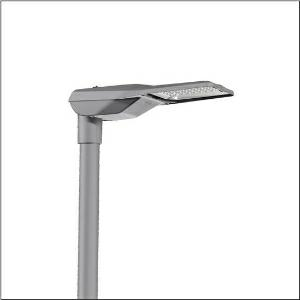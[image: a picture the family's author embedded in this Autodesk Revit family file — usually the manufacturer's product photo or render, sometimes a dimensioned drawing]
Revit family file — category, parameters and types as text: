
# Revit family: streetlight_sl_21_mini___p0_8ab_5xe2r33s08gb_ab20
name_source: partatom
category: Lighting Fixtures
units: mm (PartAtom-declared; Revit-internal decimal feet)

## family parameters
Cut with Voids When Loaded = No
Host = Face
Light Source = No
Part Type = Normal
Room Calculation Point = No
Round Connector Dimension = Use Diameter
Shared = No

## types (1)
- --- (1 x LED, 5160 lm, 40.4 W, 3000K)
    Apparent Load = 40 VA
    CIE Flux Codes = 36 71 98 100 100
    Color Rendering = 70
    Color Temperature = 3000K
    Default Elevation = 1800 mm
    Description = Streetlight SL 21 mini, mast luminaire, primary light control with lens, of PMMA, primary optical cover: cover, of toughened safety glass, transparent, light distribution: P0.8aB, light emission: direct distribution, primary light characteristic: asymmetric, installation type: post-top, side-entry, LED, High Power LED, rated luminous flux: 5.160lm, luminous efficacy: 128lm/W, light colour: 730, colour temperature: 3000K, control gear: D4i, control: pre-setting: logarithmic dimming characteristic, flexible luminous flux parameterisation, time-dependent luminous flux control, constant luminous flux control, overheat protection, mains connection: 220..240V, AC, 50/60Hz, start of lifetime: 40W, end of service life: 41W, reduction: 19W, luminaire housing, of diecast aluminium, powder-coated, Siteco® metallic grey (DB 702S), corrosivity category C5 mid according to DIN EN ISO 12944, multi-level sealing system, sealing non-destructively replaceable, inclination adjustable: 0°, 5°, 10°, 15°, please order mast flange separately, length: 628mm, width: 235mm, height: 110mm, mast flange for spigot size: 42mm (side-entry): 5XC10008XM4, 60/48mm (side-entry/post-top): 5XC10108XM2, 76/60mm (side-entry/post-top): 5XC10108XM1, mounting height: 4..8m, Smart Interface above, protection rating (complete): IP66, insulation class (complete): insulation class II (safety insulation), certification: CE, ENEC, ENEC+, VDE, impact resistance: IK10, permissible operating ambient temperature for outdoor applications: -40..+50°C, standard-compliant lighting for roads and squares, packaging unit: 1 piece

Light Distribution: P0.8aB
    Height = 110 mm
    Lamp = 1 x LED
    Lamp Light Flux = 5160 lm
    Lamp Power = 40.4 W
    Lamp count = 1
    Length = 625 mm
    Luminous efficacy = 128 lm/W
    Manufacturer = Siteco
    ModVariant = No
    Model = 5XE2R33S08GB
    Number of Poles = 1
    OnlyDefault = Yes
    Power Factor = 1
    Product Name = Streetlight SL 21 mini | P0.8aB
    Product group = mast luminaire | pylon top
    ProductGroupID = 6100
    Protection Class = Protection class II
    Protection Degree = IP 66
    RLX_Detail_Level = 1
    RLX_Emergency_Light_Flux = 0 lm
    RLX_Emergency_Type = 0
    RLX_Emergency_Type_DB = No
    RlxData = <blob elided: 91781 chars, md5=c8cf1a39>
    Socket = socket
    Standby Power = 0 W
    System Light Flux = 5160 lm
    System Power = 40 W
    Type Comments = factory setting: luminous flux: 100 % | dim-lin: 254 | 812 mA
    Type Image = l_1003515.jpg
    URL = http://relux.com
    VarID = @adj_096159
    Voltage = 0 V
    Weight = 0.00 kg
    Width = 234 mm

## geometry (parser evidence)
native form markers: Blend x4, Sweep x10
no freeform markers — native parametric forms only
